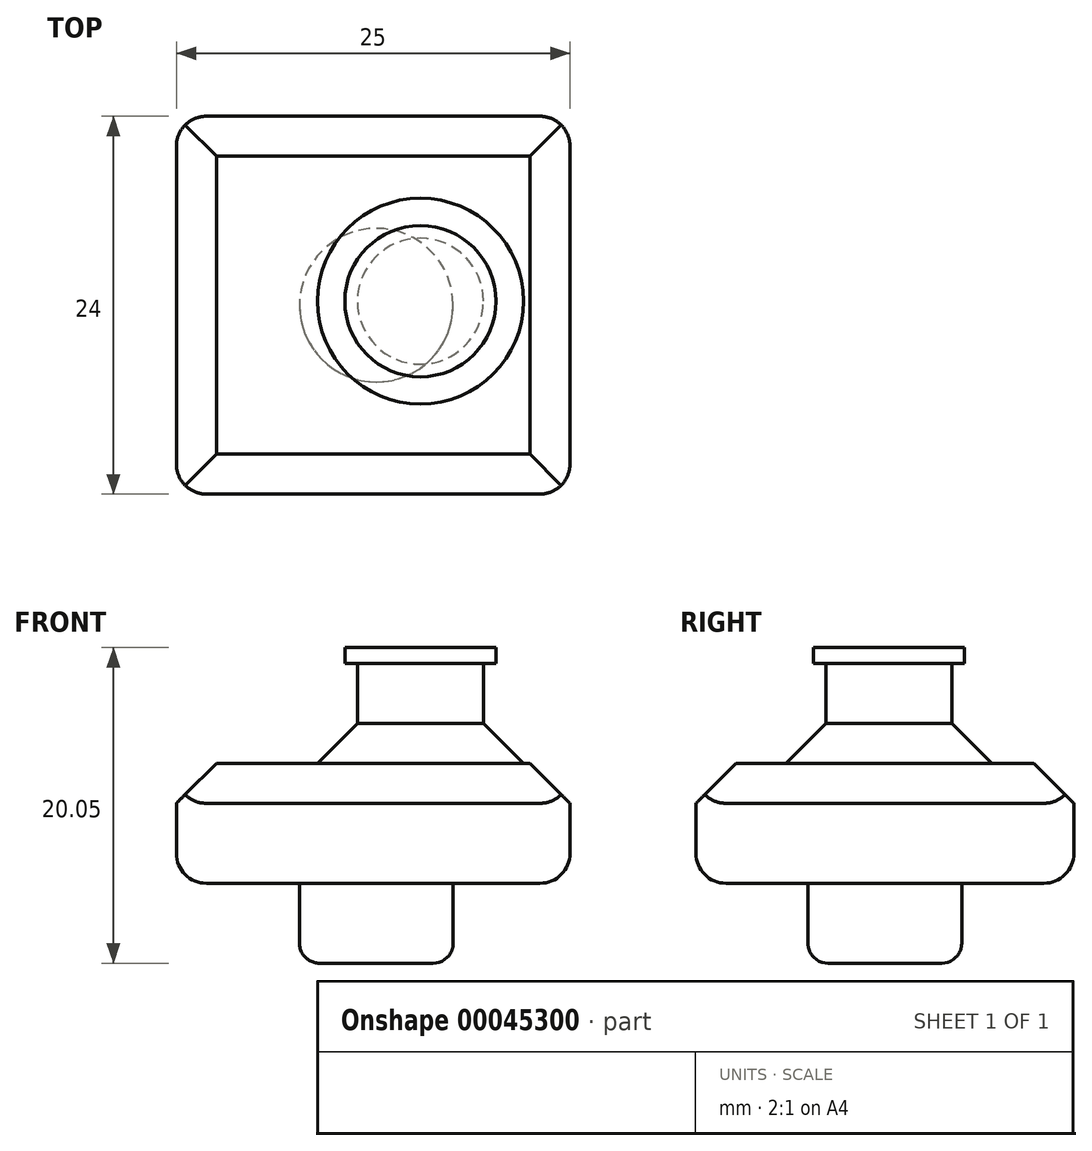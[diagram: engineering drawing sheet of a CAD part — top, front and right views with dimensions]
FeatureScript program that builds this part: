
annotation { "Feature Type Name" : "Feature", "Feature Type Description" : "" }
export const myFeature = defineFeature(function(context is Context, id is Id, definition is map)
    precondition{}
    {
        {
            var Q0;
            Q0=qCreatedBy(makeId("Top.planeOp"),FACE);
            var sketch = newSketch(context, id + "F0", { "sketchPlane" : qUnion([Q0])});
            skLineSegment(sketch, "E0.bottom", {"start": v(0, 0) * mm, "end": v(25, 0) * mm});
            skLineSegment(sketch, "E0.top", {"start": v(0, 24) * mm, "end": v(25, 24) * mm});
            skLineSegment(sketch, "E0.left", {"start": v(0, 0) * mm, "end": v(0, 24) * mm});
            skLineSegment(sketch, "E0.right", {"start": v(25, 0) * mm, "end": v(25, 24) * mm});
            skSolve(sketch);
        }
        {
            var Q0;
            Q0=makeQuery(id+"F0.imprint","IMPRINT",FACE,{"disambiguationData":[TD([[makeQuery(id+"F0.imprint","IMPRINT",EDGE,{"derivedFrom":sQuery(id+"F0.wireOp",EDGE,"E0.bottom")}),1.0]])]});
            extrude(context, id + "F1", {"entities" : qUnion([Q0]), "depth" : 7.62 * mm});
        }
        {
            var Q0;
            Q0=makeQuery(id+"F1.opExtrude","CAP_FACE",FACE,{"disambiguationData":[OSD([sQuery(id+"F0.wireOp",EDGE,"E0.bottom"),sQuery(id+"F0.wireOp",EDGE,"E0.top"),sQuery(id+"F0.wireOp",EDGE,"E0.left"),sQuery(id+"F0.wireOp",EDGE,"E0.right")])],"isStart":false});
            var sketch = newSketch(context, id + "F2", { "sketchPlane" : qUnion([Q0])});
            skCircle(sketch, "E1", {"center": v(15.5, 12.25) * mm, "radius": 4 * mm});
            skSolve(sketch);
        }
        {
            var Q0;
            Q0=makeQuery(id+"F2.imprint","IMPRINT",FACE,{"disambiguationData":[TD([[makeQuery(id+"F2.imprint","IMPRINT",EDGE,{"derivedFrom":sQuery(id+"F2.wireOp",EDGE,"E1")}),1.0]])]});
            extrude(context, id + "F3", {"entities" : qUnion([Q0]), "operationType" : NewBodyOperationType.ADD, "depth" : 6.35 * mm});
        }
        {
            var Q0;
            Q0=makeQuery(id+"F3.opExtrude","CAP_FACE",FACE,{"disambiguationData":[OSD([sQuery(id+"F2.wireOp",EDGE,"E1")])],"isStart":false});
            var sketch = newSketch(context, id + "F4", { "sketchPlane" : qUnion([Q0])});
            skCircle(sketch, "E2", {"center": v(15.5, 12.25) * mm, "radius": 4.8 * mm});
            skSolve(sketch);
        }
        {
            var Q0;
            Q0=makeQuery(id+"F4.imprint","IMPRINT",FACE,{"disambiguationData":[TD([[makeQuery(id+"F4.imprint","IMPRINT",EDGE,{"derivedFrom":sQuery(id+"F4.wireOp",EDGE,"E2")}),1.0]])]});
            var Q1;
            Q1=makeQuery(id+"F4.imprint","IMPRINT",FACE,{"disambiguationData":[TD([[makeQuery(id+"F4.imprint","IMPRINT",EDGE,{"derivedFrom":makeQuery(id+"F3.opExtrude","CAP_EDGE",EDGE,{"disambiguationData":[OSD([sQuery(id+"F2.wireOp",EDGE,"E1")])],"isStart":false})}),1.0]])]});
            extrude(context, id + "F5", {"entities" : qUnion([Q0, Q1]), "operationType" : NewBodyOperationType.ADD, "depth" : 1 * mm});
        }
        {
            var Q0;
            Q0=makeQuery(id+"F1.opExtrude","CAP_FACE",FACE,{"disambiguationData":[OSD([sQuery(id+"F0.wireOp",EDGE,"E0.bottom"),sQuery(id+"F0.wireOp",EDGE,"E0.top"),sQuery(id+"F0.wireOp",EDGE,"E0.left"),sQuery(id+"F0.wireOp",EDGE,"E0.right")])],"isStart":false});
            chamfer(context, id + "F6", {"entities" : qUnion([Q0]), "width" : 2.54 * mm, "tangentPropagation" : true});
        }
        {
            var Q0;
            Q0=makeQuery(id+"F1.opExtrude","CAP_FACE",FACE,{"disambiguationData":[OSD([sQuery(id+"F0.wireOp",EDGE,"E0.bottom"),sQuery(id+"F0.wireOp",EDGE,"E0.top"),sQuery(id+"F0.wireOp",EDGE,"E0.left"),sQuery(id+"F0.wireOp",EDGE,"E0.right")])],"isStart":true});
            var Q1;
            Q1=makeQuery(id+"F1.opExtrude","SWEPT_EDGE",EDGE,{"disambiguationData":[OSD([sQuery(id+"F0.wireOp",EDGE,"E0.top"),sQuery(id+"F0.wireOp",EDGE,"E0.right")])]});
            var Q2;
            Q2=makeQuery(id+"F1.opExtrude","SWEPT_EDGE",EDGE,{"disambiguationData":[OSD([sQuery(id+"F0.wireOp",EDGE,"E0.bottom"),sQuery(id+"F0.wireOp",EDGE,"E0.right")])]});
            var Q3;
            Q3=makeQuery(id+"F1.opExtrude","SWEPT_EDGE",EDGE,{"disambiguationData":[OSD([sQuery(id+"F0.wireOp",EDGE,"E0.bottom"),sQuery(id+"F0.wireOp",EDGE,"E0.left")])]});
            var Q4;
            Q4=makeQuery(id+"F1.opExtrude","SWEPT_EDGE",EDGE,{"disambiguationData":[OSD([sQuery(id+"F0.wireOp",EDGE,"E0.top"),sQuery(id+"F0.wireOp",EDGE,"E0.left")])]});
            fillet(context, id + "F7", {"entities" : qUnion([Q0, Q1, Q2, Q3, Q4]), "radius" : 1.9 * mm, "tangentPropagation" : true, "allowEdgeOverflow" : false});
        }
        {
            var Q0;
            Q0=makeQuery(id+"F1.opExtrude","CAP_FACE",FACE,{"disambiguationData":[OSD([sQuery(id+"F0.wireOp",EDGE,"E0.bottom"),sQuery(id+"F0.wireOp",EDGE,"E0.top"),sQuery(id+"F0.wireOp",EDGE,"E0.left"),sQuery(id+"F0.wireOp",EDGE,"E0.right")])],"isStart":true});
            var sketch = newSketch(context, id + "F8", { "sketchPlane" : qUnion([Q0])});
            skCircle(sketch, "E3", {"center": v(12.7, -12) * mm, "radius": 4.88 * mm});
            skLineSegment(sketch, "E4", {"start": v(23.1, -12) * mm, "end": v(12.7, -12) * mm, "construction": true});
            skSolve(sketch);
        }
        {
            var Q0;
            Q0=makeQuery(id+"F8.imprint","IMPRINT",FACE,{"disambiguationData":[TD([[makeQuery(id+"F8.imprint","IMPRINT",EDGE,{"derivedFrom":sQuery(id+"F8.wireOp",EDGE,"E3")}),1.0]])]});
            var Q1;
            Q1=sQuery(id+"F8.wireOp",EDGE,"E4");
            var Q2;
            Q2=sQuery(id+"F8.wireOp",EDGE,"E3");
            extrude(context, id + "F9", {"entities" : qUnion([Q0]), "operationType" : NewBodyOperationType.ADD, "surfaceEntities" : qUnion([Q1, Q2]), "depth" : 5.08 * mm});
        }
        {
            var Q0;
            Q0=makeQuery(id+"F9.opExtrude","CAP_FACE",FACE,{"disambiguationData":[OSD([sQuery(id+"F8.wireOp",EDGE,"E3")])],"isStart":false});
            fillet(context, id + "F10", {"entities" : qUnion([Q0]), "radius" : 1.27 * mm, "tangentPropagation" : true, "allowEdgeOverflow" : false});
        }
    });
